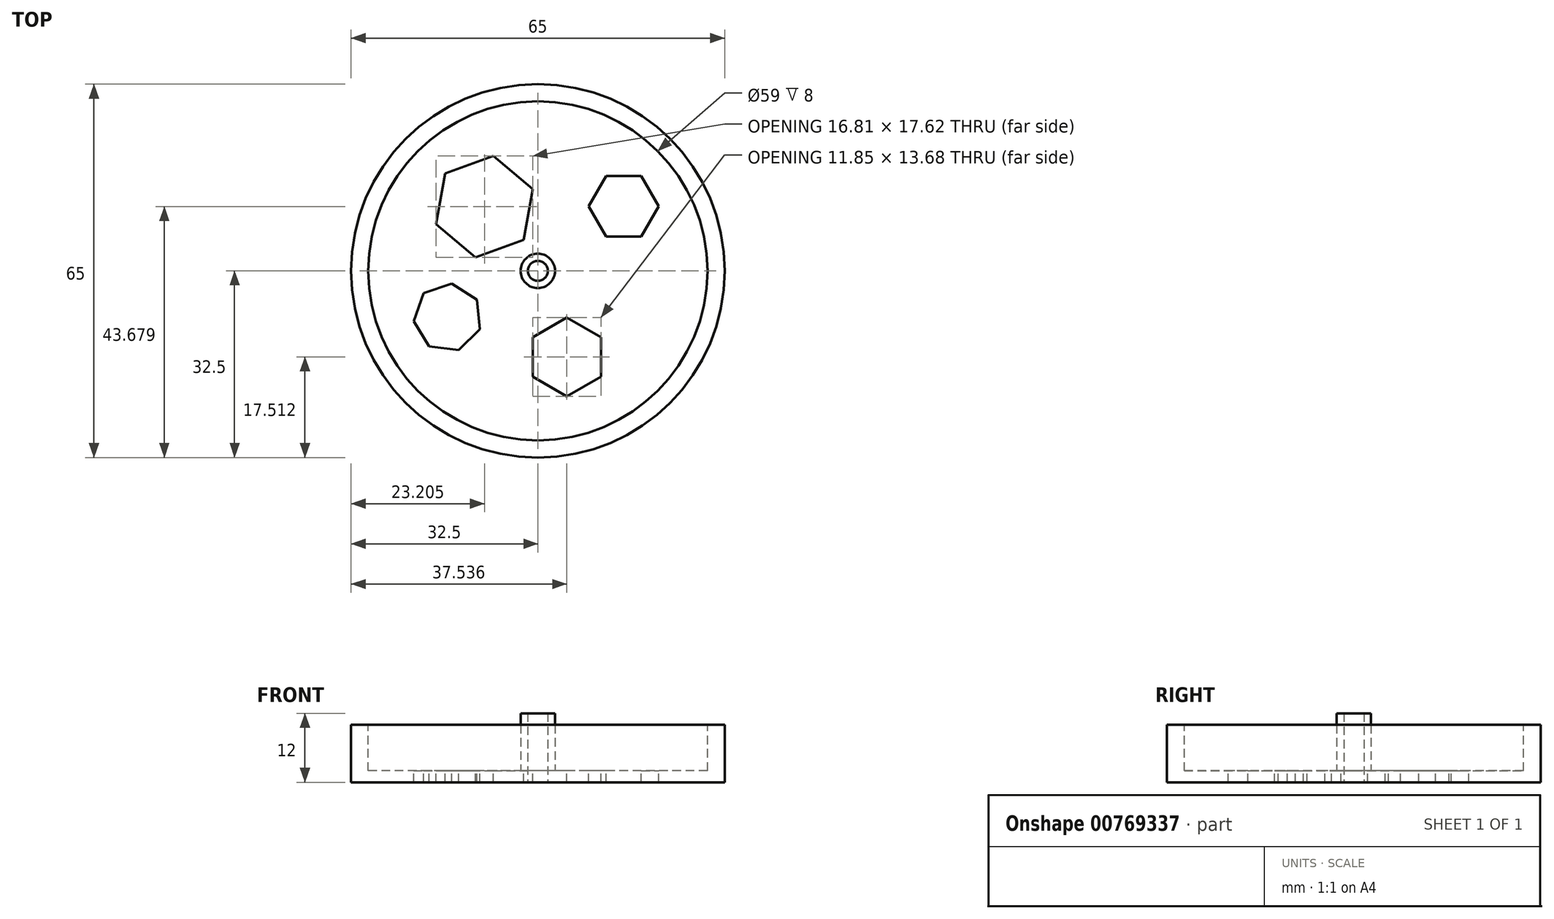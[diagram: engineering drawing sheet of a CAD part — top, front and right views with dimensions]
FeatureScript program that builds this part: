
annotation { "Feature Type Name" : "Feature", "Feature Type Description" : "" }
export const myFeature = defineFeature(function(context is Context, id is Id, definition is map)
    precondition{}
    {
        {
            var Q0;
            Q0=qCreatedBy(makeId("Top.planeOp"),FACE);
            var sketch = newSketch(context, id + "F0", { "sketchPlane" : qUnion([Q0])});
            skCircle(sketch, "E0", {"center": v(0, 0) * mm, "radius": 32.5 * mm});
            skSolve(sketch);
        }
        {
            var Q0;
            Q0=makeQuery(id+"F0.imprint","IMPRINT",FACE,{"disambiguationData":[TD([[makeQuery(id+"F0.imprint","IMPRINT",EDGE,{"derivedFrom":sQuery(id+"F0.wireOp",EDGE,"E0")}),1.0]])]});
            extrude(context, id + "F1", {"entities" : qUnion([Q0]), "depth" : 10 * mm, "offsetDistance" : 25 * mm});
        }
        {
            var Q0;
            Q0=makeQuery(id+"F1.opExtrude","CAP_FACE",FACE,{"disambiguationData":[OSD([sQuery(id+"F0.wireOp",EDGE,"E0")])],"isStart":false});
            var sketch = newSketch(context, id + "F2", { "sketchPlane" : qUnion([Q0])});
            skCircle(sketch, "E1", {"center": v(0, 0) * mm, "radius": 29.5 * mm});
            skSolve(sketch);
        }
        {
            var Q0;
            Q0 = qSketchRegion(id + "F2", true);
            extrude(context, id + "F3", {"entities" : qUnion([Q0]), "operationType" : NewBodyOperationType.REMOVE, "oppositeDirection" : true, "depth" : 8 * mm, "offsetDistance" : 25 * mm});
        }
        {
            var Q0;
            Q0=makeQuery(id+"F3.boolean.opBoolean","COPY",FACE,{"derivedFrom":makeQuery(id+"F3.opExtrude","CAP_FACE",FACE,{"disambiguationData":[OSD([sQuery(id+"F2.wireOp",EDGE,"E1")])],"isStart":false})});
            var sketch = newSketch(context, id + "F4", { "sketchPlane" : qUnion([Q0])});
            skCircle(sketch, "E2", {"center": v(0, 0) * mm, "radius": 3 * mm});
            skSolve(sketch);
        }
        {
            var Q0;
            Q0=sQuery(id+"F4.wireOp",EDGE,"E2");
            extrude(context, id + "F5", {"bodyType" : ToolBodyType.SURFACE, "surfaceEntities" : qUnion([Q0]), "depth" : 10 * mm, "offsetDistance" : 25 * mm});
        }
        {
            var Q0;
            Q0=sQuery(id+"F0.wireOp",VERTEX,"E0.center");
            var Q1;
            Q1=makeQuery(id+"F1.opExtrude","SWEPT_BODY",BODY,{"disambiguationData":[OSD([sQuery(id+"F0.wireOp",EDGE,"E0")])]});
            hole(context, id + "F6", {"style" : HoleStyle.SIMPLE, "endStyle" : HoleEndStyle.THROUGH, "oppositeDirection" : true, "holeDiameter" : 3.5 * mm, "majorDiameter" : 5 * mm, "isTappedThrough" : true, "tappedDepth" : 12 * mm, "tapClearance" : 3, "locations" : qUnion([Q0]), "scope" : qUnion([Q1])});
        }
        {
            var Q0;
            Q0=makeQuery(id+"F4.imprint","IMPRINT",FACE,{"disambiguationData":[TD([[makeQuery(id+"F4.imprint","IMPRINT",EDGE,{"derivedFrom":sQuery(id+"F4.wireOp",EDGE,"E2")}),-1.0]])]});
            var sketch = newSketch(context, id + "F7", { "sketchPlane" : qUnion([Q0])});
            skCircle(sketch, "E3.cCircle", {"center": v(-9.3, 11.18) * mm, "radius": 7.75 * mm, "construction": true});
            skLineSegment(sketch, "E3.0", {"start": v(-16.15, 16.93) * mm, "end": v(-7.74, 19.99) * mm});
            skLineSegment(sketch, "E3.1", {"start": v(-7.74, 19.99) * mm, "end": v(-0.89, 14.24) * mm});
            skLineSegment(sketch, "E3.2", {"start": v(-0.89, 14.24) * mm, "end": v(-2.44, 5.43) * mm});
            skLineSegment(sketch, "E3.3", {"start": v(-2.44, 5.43) * mm, "end": v(-10.85, 2.37) * mm});
            skLineSegment(sketch, "E3.4", {"start": v(-10.85, 2.37) * mm, "end": v(-17.7, 8.12) * mm});
            skLineSegment(sketch, "E3.5", {"start": v(-17.7, 8.12) * mm, "end": v(-16.15, 16.93) * mm});
            skPoint(sketch, "E3.0.midPoint", {"position": v(-11.94, 18.46) * mm});
            skCircle(sketch, "E4.cCircle", {"center": v(5.04, -14.99) * mm, "radius": 5.92 * mm, "construction": true});
            skLineSegment(sketch, "E4.0", {"start": v(-0.89, -18.4) * mm, "end": v(-0.89, -11.57) * mm});
            skLineSegment(sketch, "E4.1", {"start": v(-0.89, -11.57) * mm, "end": v(5.04, -8.15) * mm});
            skLineSegment(sketch, "E4.2", {"start": v(5.04, -8.15) * mm, "end": v(10.96, -11.57) * mm});
            skLineSegment(sketch, "E4.3", {"start": v(10.96, -11.57) * mm, "end": v(10.96, -18.4) * mm});
            skLineSegment(sketch, "E4.4", {"start": v(10.96, -18.4) * mm, "end": v(5.04, -21.83) * mm});
            skLineSegment(sketch, "E4.5", {"start": v(5.04, -21.83) * mm, "end": v(-0.89, -18.4) * mm});
            skPoint(sketch, "E4.0.midPoint", {"position": v(-0.89, -14.99) * mm});
            skCircle(sketch, "E5.cCircle", {"center": v(14.94, 11.26) * mm, "radius": 5.28 * mm, "construction": true});
            skLineSegment(sketch, "E5.0", {"start": v(17.99, 5.99) * mm, "end": v(11.9, 5.99) * mm});
            skLineSegment(sketch, "E5.1", {"start": v(11.9, 5.99) * mm, "end": v(8.85, 11.26) * mm});
            skLineSegment(sketch, "E5.2", {"start": v(8.85, 11.26) * mm, "end": v(11.9, 16.54) * mm});
            skLineSegment(sketch, "E5.3", {"start": v(11.9, 16.54) * mm, "end": v(17.99, 16.54) * mm});
            skLineSegment(sketch, "E5.4", {"start": v(17.99, 16.54) * mm, "end": v(21.04, 11.26) * mm});
            skLineSegment(sketch, "E5.5", {"start": v(21.04, 11.26) * mm, "end": v(17.99, 5.99) * mm});
            skPoint(sketch, "E5.0.midPoint", {"position": v(14.94, 5.99) * mm});
            skCircle(sketch, "E6.cCircle", {"center": v(-15.7, -8.15) * mm, "radius": 5.36 * mm, "construction": true});
            skLineSegment(sketch, "E6.0", {"start": v(-10.1, -10.17) * mm, "end": v(-13.79, -13.78) * mm});
            skLineSegment(sketch, "E6.1", {"start": v(-13.79, -13.78) * mm, "end": v(-18.9, -13.15) * mm});
            skLineSegment(sketch, "E6.2", {"start": v(-18.9, -13.15) * mm, "end": v(-21.6, -8.75) * mm});
            skLineSegment(sketch, "E6.3", {"start": v(-21.6, -8.75) * mm, "end": v(-19.85, -3.9) * mm});
            skLineSegment(sketch, "E6.4", {"start": v(-19.85, -3.9) * mm, "end": v(-14.96, -2.25) * mm});
            skLineSegment(sketch, "E6.5", {"start": v(-14.96, -2.25) * mm, "end": v(-10.62, -5.04) * mm});
            skLineSegment(sketch, "E6.6", {"start": v(-10.62, -5.04) * mm, "end": v(-10.1, -10.17) * mm});
            skPoint(sketch, "E6.0.midPoint", {"position": v(-11.94, -11.97) * mm});
            skSolve(sketch);
        }
        {
            var Q0;
            Q0=makeQuery(id+"F7.imprint","IMPRINT",FACE,{"disambiguationData":[TD([[makeQuery(id+"F7.imprint","IMPRINT",EDGE,{"derivedFrom":sQuery(id+"F7.wireOp",EDGE,"E3.0")}),-1.0]])]});
            extrude(context, id + "F8", {"entities" : qUnion([Q0]), "operationType" : NewBodyOperationType.REMOVE, "endBound" : BoundingType.UP_TO_NEXT, "oppositeDirection" : true, "depth" : 25 * mm, "offsetDistance" : 25 * mm});
        }
        {
            var Q0;
            Q0=makeQuery(id+"F7.imprint","IMPRINT",FACE,{"disambiguationData":[TD([[makeQuery(id+"F7.imprint","IMPRINT",EDGE,{"derivedFrom":sQuery(id+"F7.wireOp",EDGE,"E4.0")}),-1.0]])]});
            extrude(context, id + "F9", {"entities" : qUnion([Q0]), "operationType" : NewBodyOperationType.REMOVE, "endBound" : BoundingType.UP_TO_NEXT, "oppositeDirection" : true, "depth" : 25 * mm, "offsetDistance" : 25 * mm});
        }
        {
            var Q0;
            Q0=makeQuery(id+"F7.imprint","IMPRINT",FACE,{"disambiguationData":[TD([[makeQuery(id+"F7.imprint","IMPRINT",EDGE,{"derivedFrom":sQuery(id+"F7.wireOp",EDGE,"E6.0")}),-1.0]])]});
            extrude(context, id + "F10", {"entities" : qUnion([Q0]), "operationType" : NewBodyOperationType.REMOVE, "endBound" : BoundingType.UP_TO_NEXT, "oppositeDirection" : true, "depth" : 25 * mm, "offsetDistance" : 25 * mm});
        }
        {
            var Q0;
            Q0=makeQuery(id+"F7.imprint","IMPRINT",FACE,{"disambiguationData":[TD([[makeQuery(id+"F7.imprint","IMPRINT",EDGE,{"derivedFrom":sQuery(id+"F7.wireOp",EDGE,"E5.0")}),-1.0]])]});
            extrude(context, id + "F11", {"entities" : qUnion([Q0]), "operationType" : NewBodyOperationType.REMOVE, "endBound" : BoundingType.UP_TO_NEXT, "oppositeDirection" : true, "depth" : 25 * mm, "offsetDistance" : 25 * mm});
        }
        {
            var Q0;
            Q0=makeQuery(id+"F4.imprint","IMPRINT",FACE,{"disambiguationData":[TD([[makeQuery(id+"F4.imprint","IMPRINT",EDGE,{"derivedFrom":sQuery(id+"F4.wireOp",EDGE,"E2")}),1.0]])]});
            extrude(context, id + "F12", {"entities" : qUnion([Q0]), "operationType" : NewBodyOperationType.ADD, "depth" : 10 * mm, "offsetDistance" : 25 * mm});
        }
        {
            var Q0;
            Q0=makeQuery(id+"F12.opExtrude","CAP_FACE",FACE,{"disambiguationData":[OSD([sQuery(id+"F4.wireOp",EDGE,"E2")])],"isStart":false});
            var sketch = newSketch(context, id + "F13", { "sketchPlane" : qUnion([Q0])});
            skPoint(sketch, "E7", {"position": v(0, 0) * mm});
            skSolve(sketch);
        }
        {
            var Q0;
            Q0=sQuery(id+"F13.wireOp",VERTEX,"E7");
            var Q1;
            Q1=makeQuery(id+"F1.opExtrude","SWEPT_BODY",BODY,{"disambiguationData":[OSD([sQuery(id+"F0.wireOp",EDGE,"E0")])]});
            hole(context, id + "F14", {"style" : HoleStyle.SIMPLE, "endStyle" : HoleEndStyle.THROUGH, "holeDiameter" : 3.5 * mm, "majorDiameter" : 5 * mm, "isTappedThrough" : true, "tappedDepth" : 12 * mm, "tapClearance" : 3, "locations" : qUnion([Q0]), "scope" : qUnion([Q1])});
        }
    });
